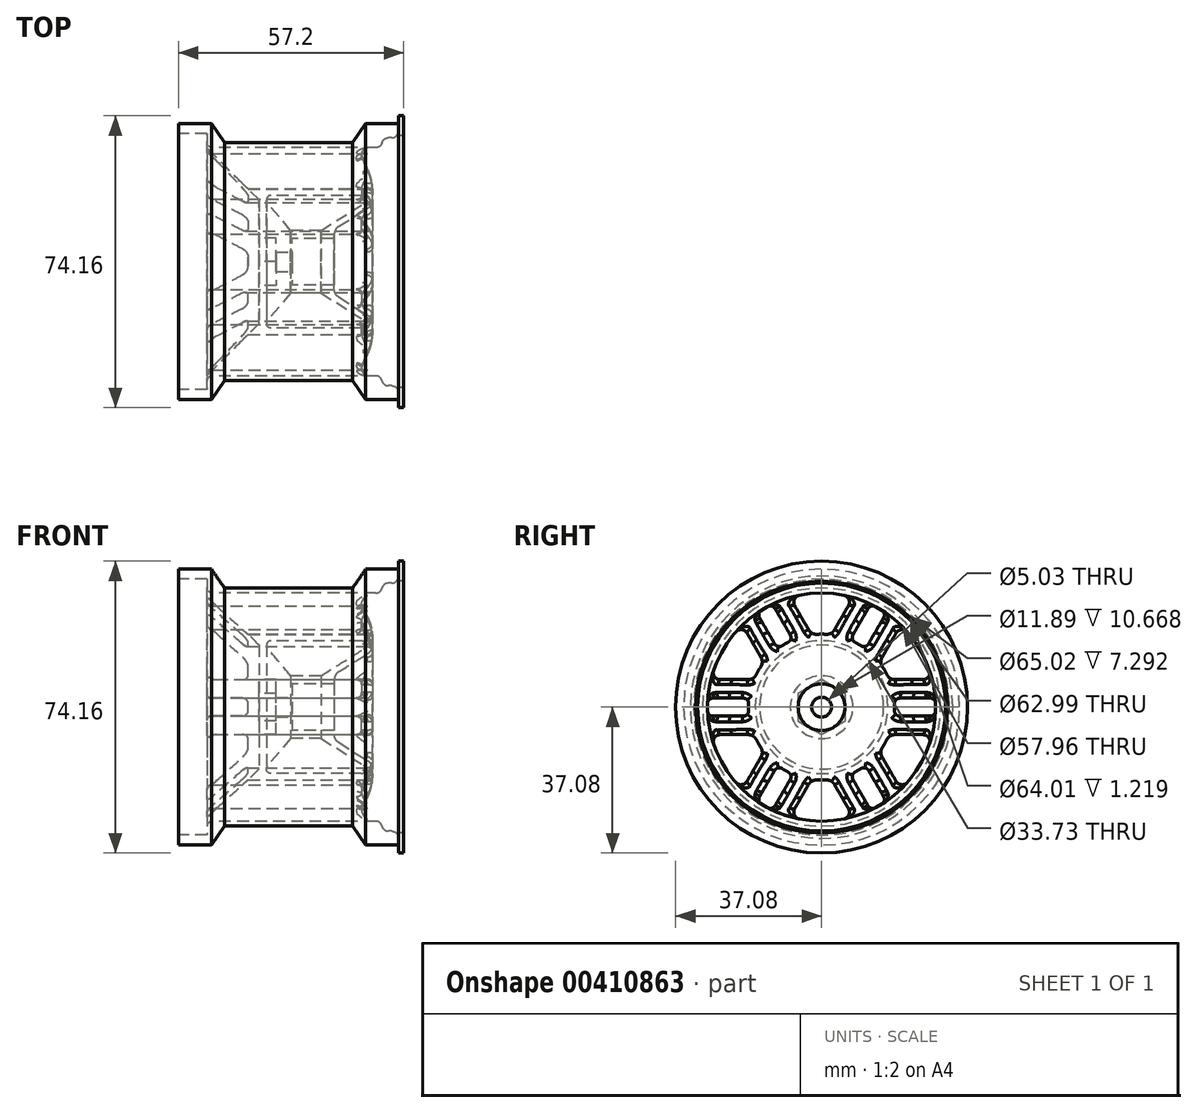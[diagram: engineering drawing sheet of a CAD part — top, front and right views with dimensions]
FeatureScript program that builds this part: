
annotation { "Feature Type Name" : "Feature", "Feature Type Description" : "" }
export const myFeature = defineFeature(function(context is Context, id is Id, definition is map)
    precondition{}
    {
        {
            var Q0;
            Q0=qCreatedBy(makeId("Front.planeOp"),FACE);
            var sketch = newSketch(context, id + "F0", { "sketchPlane" : qUnion([Q0])});
            skLineSegment(sketch, "E0.top", {"start": v(-20.52, 0) * mm, "end": v(36.68, 0) * mm});
            skLineSegment(sketch, "E0.left", {"start": v(-20.52, 35.05) * mm, "end": v(-20.52, 0) * mm});
            skLineSegment(sketch, "E0.right", {"start": v(36.68, 35.05) * mm, "end": v(36.68, 0) * mm});
            skLineSegment(sketch, "E1.top", {"start": v(36.68, 37.08) * mm, "end": v(35.46, 37.08) * mm});
            skLineSegment(sketch, "E1.left", {"start": v(36.68, 35.05) * mm, "end": v(36.68, 37.08) * mm});
            skLineSegment(sketch, "E1.right", {"start": v(35.46, 35.05) * mm, "end": v(35.46, 37.08) * mm});
            skLineSegment(sketch, "E2", {"start": v(35.46, 35.05) * mm, "end": v(36.68, 35.05) * mm, "construction": true});
            skPoint(sketch, "E3", {"position": v(0, 0) * mm});
            skLineSegment(sketch, "E4", {"start": v(-20.52, 35.05) * mm, "end": v(-12.14, 35.05) * mm});
            skLineSegment(sketch, "E5", {"start": v(-12.14, 35.05) * mm, "end": v(-8.76, 30.23) * mm});
            skLineSegment(sketch, "E6", {"start": v(-8.76, 30.23) * mm, "end": v(23.7, 30.23) * mm});
            skLineSegment(sketch, "E7", {"start": v(23.7, 30.23) * mm, "end": v(27.08, 35.05) * mm});
            skLineSegment(sketch, "E8", {"start": v(27.08, 35.05) * mm, "end": v(35.46, 35.05) * mm});
            skLineSegment(sketch, "E9", {"start": v(7.47, 30.23) * mm, "end": v(7.47, 0) * mm, "construction": true});
            skSolve(sketch);
        }
        {
            var Q0;
            Q0=makeQuery(id+"F0.imprint","IMPRINT",FACE,{"disambiguationData":[TD([[makeQuery(id+"F0.imprint","IMPRINT",EDGE,{"derivedFrom":sQuery(id+"F0.wireOp",EDGE,"E0.top")}),1.0]])]});
            var Q1;
            Q1=sQuery(id+"F0.wireOp",EDGE,"E0.top");
            revolve(context, id + "F1", {"entities" : qUnion([Q0]), "axis" : qUnion([Q1]), "revolveType" : RevolveType.FULL});
        }
        {
            var Q0;
            Q0=qCreatedBy(makeId("Right.planeOp"),FACE);
            cPlane(context, id + "F2", {"entities" : qUnion([Q0]), "cplaneType" : CPlaneType.OFFSET, "offset" : 13.2 * mm, "width" : 152.4 * mm, "height" : 152.4 * mm});
        }
        {
            var Q0;
            Q0=qCreatedBy(id+"F2.planeOp",FACE);
            var sketch = newSketch(context, id + "F3", { "sketchPlane" : qUnion([Q0])});
            skPoint(sketch, "E10", {"position": v(0, 0) * mm});
            skSolve(sketch);
        }
        {
            var Q0;
            Q0=sQuery(id+"F3.wireOp",VERTEX,"E10");
            var Q1;
            Q1=makeQuery(id+"F1.opRevolve","SWEPT_BODY",BODY,{"disambiguationData":[OSD([sQuery(id+"F0.wireOp",EDGE,"E0.top"),sQuery(id+"F0.wireOp",EDGE,"E0.left"),sQuery(id+"F0.wireOp",EDGE,"E0.right"),sQuery(id+"F0.wireOp",EDGE,"E1.top"),sQuery(id+"F0.wireOp",EDGE,"E1.left"),sQuery(id+"F0.wireOp",EDGE,"E1.right"),sQuery(id+"F0.wireOp",EDGE,"E4"),sQuery(id+"F0.wireOp",EDGE,"E5"),sQuery(id+"F0.wireOp",EDGE,"E6"),sQuery(id+"F0.wireOp",EDGE,"E7"),sQuery(id+"F0.wireOp",EDGE,"E8")])]});
            hole(context, id + "F4", {"style" : HoleStyle.SIMPLE, "endStyle" : HoleEndStyle.THROUGH, "oppositeDirection" : true, "holeDiameter" : 11.9 * mm, "locations" : qUnion([Q0]), "scope" : qUnion([Q1]), "isTappedThrough" : true});
        }
        {
            var Q0;
            Q0=sQuery(id+"F3.wireOp",VERTEX,"E10");
            var Q1;
            Q1=makeQuery(id+"F1.opRevolve","SWEPT_BODY",BODY,{"disambiguationData":[OSD([sQuery(id+"F0.wireOp",EDGE,"E0.top"),sQuery(id+"F0.wireOp",EDGE,"E0.left"),sQuery(id+"F0.wireOp",EDGE,"E0.right"),sQuery(id+"F0.wireOp",EDGE,"E1.top"),sQuery(id+"F0.wireOp",EDGE,"E1.left"),sQuery(id+"F0.wireOp",EDGE,"E1.right"),sQuery(id+"F0.wireOp",EDGE,"E4"),sQuery(id+"F0.wireOp",EDGE,"E5"),sQuery(id+"F0.wireOp",EDGE,"E6"),sQuery(id+"F0.wireOp",EDGE,"E7"),sQuery(id+"F0.wireOp",EDGE,"E8")])]});
            hole(context, id + "F5", {"style" : HoleStyle.C_BORE, "endStyle" : HoleEndStyle.THROUGH, "holeDiameter" : 5.03 * mm, "cBoreDiameter" : 11.9 * mm, "cBoreDepth" : 4.83 * mm, "locations" : qUnion([Q0]), "scope" : qUnion([Q1]), "isTappedThrough" : true});
        }
        {
            var Q0;
            Q0=qCreatedBy(makeId("Front.planeOp"),FACE);
            var sketch = newSketch(context, id + "F6", { "sketchPlane" : qUnion([Q0])});
            skLineSegment(sketch, "E11.bottom", {"start": v(0, 0) * mm, "end": v(-20.52, 0) * mm});
            skLineSegment(sketch, "E11.left", {"start": v(0, 0) * mm, "end": v(0, 15.75) * mm});
            skLineSegment(sketch, "E11.right", {"start": v(-20.52, 0) * mm, "end": v(-20.52, 32.51) * mm});
            skLineSegment(sketch, "E12", {"start": v(-20.52, 32.51) * mm, "end": v(-20.52, 35.05) * mm, "construction": true});
            skPoint(sketch, "E13.visualSharp", {"position": v(0, 15.75) * mm});
            skPoint(sketch, "E14.visualSharp", {"position": v(-20.52, 32.51) * mm});
            skLineSegment(sketch, "E15", {"start": v(-13.23, 28.98) * mm, "end": v(0, 15.75) * mm});
            skLineSegment(sketch, "E16", {"start": v(-20.52, 32.51) * mm, "end": v(-13.23, 32.51) * mm});
            skLineSegment(sketch, "E17", {"start": v(-13.23, 32.51) * mm, "end": v(-13.23, 28.98) * mm});
            skSolve(sketch);
        }
        {
            var Q0;
            Q0=qSketchRegion(id+"F6",true);
            var Q1;
            Q1=sQuery(id+"F6.wireOp",EDGE,"E11.bottom");
            revolve(context, id + "F7", {"operationType" : NewBodyOperationType.REMOVE, "entities" : qUnion([Q0]), "axis" : qUnion([Q1]), "revolveType" : RevolveType.FULL, "oppositeDirection" : true});
        }
        {
            var Q0;
            Q0=qCreatedBy(makeId("Right.planeOp"),FACE);
            var sketch = newSketch(context, id + "F8", { "sketchPlane" : qUnion([Q0])});
            skPoint(sketch, "E18", {"position": v(0.13, 0.17) * mm});
            skLineSegment(sketch, "E19", {"start": v(6.05, -3.5) * mm, "end": v(6.05, 3.5) * mm});
            skLineSegment(sketch, "E20", {"start": v(0, 0) * mm, "end": v(6.05, 0) * mm, "construction": true});
            skLineSegment(sketch, "E21.1.0", {"start": v(6.05, 3.5) * mm, "end": v(0, 6.98) * mm});
            skLineSegment(sketch, "E21.2.0", {"start": v(0, 6.98) * mm, "end": v(-6.05, 3.5) * mm});
            skLineSegment(sketch, "E21.3.0", {"start": v(-6.05, 3.5) * mm, "end": v(-6.05, -3.5) * mm});
            skLineSegment(sketch, "E21.4.0", {"start": v(-6.05, -3.5) * mm, "end": v(0, -6.98) * mm});
            skLineSegment(sketch, "E21.5.0", {"start": v(0, -6.98) * mm, "end": v(6.05, -3.5) * mm});
            skPoint(sketch, "E21.center", {"position": v(0, 0) * mm});
            skPoint(sketch, "E22.orphan", {"position": v(1.46, 7.82) * mm});
            skPoint(sketch, "E23.orphan", {"position": v(6.05, 5.17) * mm});
            skPoint(sketch, "E24.orphan", {"position": v(6.05, -5.17) * mm});
            skPoint(sketch, "E25.orphan", {"position": v(-1.46, 7.82) * mm});
            skPoint(sketch, "E26.orphan", {"position": v(7.5, 2.65) * mm});
            skPoint(sketch, "E27.orphan", {"position": v(7.5, -2.65) * mm});
            skPoint(sketch, "E28.orphan", {"position": v(1.46, -7.82) * mm});
            skPoint(sketch, "E29.orphan", {"position": v(-1.46, -7.82) * mm});
            skPoint(sketch, "E30.orphan", {"position": v(-6.05, -5.17) * mm});
            skPoint(sketch, "E31.orphan", {"position": v(-7.5, -2.65) * mm});
            skPoint(sketch, "E32.orphan", {"position": v(-7.5, 2.65) * mm});
            skPoint(sketch, "E33.orphan", {"position": v(-6.05, 5.17) * mm});
            skSolve(sketch);
        }
        {
            var Q0;
            Q0=qSketchRegion(id+"F8",true);
            extrude(context, id + "F9", {"entities" : qUnion([Q0]), "operationType" : NewBodyOperationType.REMOVE, "depth" : 4.32 * mm});
        }
        {
            var Q0;
            Q0=qCreatedBy(makeId("Front.planeOp"),FACE);
            var sketch = newSketch(context, id + "F10", { "sketchPlane" : qUnion([Q0])});
            skLineSegment(sketch, "E34", {"start": v(36.68, 32) * mm, "end": v(36.68, 37.08) * mm, "construction": true});
            skLineSegment(sketch, "E35", {"start": v(36.68, 32) * mm, "end": v(35.46, 32) * mm});
            skLineSegment(sketch, "E36", {"start": v(35.46, 32) * mm, "end": v(35.32, 33.33) * mm});
            skArc(sketch, "E37", {"start": v(35.32, 33.33) * mm, "mid": v(34.9, 32.04) * mm, "end": v(33.67, 31.5) * mm});
            skLineSegment(sketch, "E38", {"start": v(33.67, 31.5) * mm, "end": v(32.8, 31.5) * mm});
            skArc(sketch, "E39", {"start": v(32.8, 31.5) * mm, "mid": v(31.79, 31.14) * mm, "end": v(31.2, 30.24) * mm});
            skArc(sketch, "E40", {"start": v(29.59, 28.98) * mm, "mid": v(30.6, 29.33) * mm, "end": v(31.2, 30.24) * mm});
            skLineSegment(sketch, "E41", {"start": v(29.59, 28.98) * mm, "end": v(27.56, 28.98) * mm});
            skArc(sketch, "E42", {"start": v(27.56, 28.98) * mm, "mid": v(26.28, 28.29) * mm, "end": v(26.17, 26.83) * mm});
            skLineSegment(sketch, "E43", {"start": v(8.38, 5.94) * mm, "end": v(19.05, 5.94) * mm, "construction": true});
            skLineSegment(sketch, "E44", {"start": v(27.55, 23.75) * mm, "end": v(26.17, 26.83) * mm});
            skLineSegment(sketch, "E45", {"start": v(36.68, 32) * mm, "end": v(36.68, 0) * mm});
            skLineSegment(sketch, "E46", {"start": v(36.68, 0) * mm, "end": v(19.05, 0) * mm});
            skLineSegment(sketch, "E47", {"start": v(31.2, 30.24) * mm, "end": v(30.65, 28.06) * mm, "construction": true});
            skLineSegment(sketch, "E48", {"start": v(19.05, 5.94) * mm, "end": v(19.05, 6.86) * mm});
            skPoint(sketch, "E49.visualSharp", {"position": v(19.05, 6.86) * mm});
            skArc(sketch, "E49.filletArc", {"start": v(28.77, 18.03) * mm, "mid": v(28.46, 20.96) * mm, "end": v(27.55, 23.75) * mm});
            skLineSegment(sketch, "E50", {"start": v(28.77, 18.03) * mm, "end": v(28.77, 15.75) * mm});
            skLineSegment(sketch, "E51", {"start": v(20.24, 9.01) * mm, "end": v(27.58, 13.6) * mm});
            skArc(sketch, "E52", {"start": v(28.77, 15.75) * mm, "mid": v(28.45, 14.52) * mm, "end": v(27.58, 13.6) * mm});
            skArc(sketch, "E53", {"start": v(20.24, 9.01) * mm, "mid": v(19.37, 8.09) * mm, "end": v(19.05, 6.86) * mm});
            skLineSegment(sketch, "E54", {"start": v(19.05, 5.94) * mm, "end": v(19.05, 0) * mm});
            skSolve(sketch);
        }
        {
            var Q0;
            Q0=qSketchRegion(id+"F10",true);
            var Q1;
            Q1=sQuery(id+"F10.wireOp",EDGE,"E46");
            revolve(context, id + "F11", {"operationType" : NewBodyOperationType.REMOVE, "entities" : qUnion([Q0]), "axis" : qUnion([Q1]), "revolveType" : RevolveType.FULL, "oppositeDirection" : true});
        }
        {
            var Q0;
            Q0=makeQuery(id+"F1.opRevolve","SWEPT_FACE",FACE,{"disambiguationData":[OSD([sQuery(id+"F0.wireOp",EDGE,"E0.right"),sQuery(id+"F0.wireOp",EDGE,"E1.left")])]});
            cPlane(context, id + "F12", {"entities" : qUnion([Q0]), "cplaneType" : CPlaneType.OFFSET, "offset" : 0 * mm, "width" : 152.4 * mm, "height" : 152.4 * mm});
        }
        {
            var Q0;
            Q0=qCreatedBy(id+"F12.planeOp",FACE);
            var sketch = newSketch(context, id + "F13", { "sketchPlane" : qUnion([Q0])});
            skLineSegment(sketch, "E55", {"start": v(6.83, 25.8) * mm, "end": v(3.28, 19.64) * mm});
            skLineSegment(sketch, "E56", {"start": v(0, 28.98) * mm, "end": v(0, 18.54) * mm, "construction": true});
            skArc(sketch, "E57", {"start": v(5.63, 28.43) * mm, "mid": v(2.83, 28.84) * mm, "end": v(0, 28.98) * mm});
            skArc(sketch, "E58", {"start": v(5.63, 28.43) * mm, "mid": v(6.9, 27.42) * mm, "end": v(6.83, 25.8) * mm});
            skLineSegment(sketch, "E59", {"start": v(0, 0) * mm, "end": v(0, 13.97) * mm, "construction": true});
            skArc(sketch, "E60", {"start": v(0, 18.54) * mm, "mid": v(0.58, 18.53) * mm, "end": v(1.15, 18.5) * mm});
            skArc(sketch, "E61.filletArc", {"start": v(1.15, 18.5) * mm, "mid": v(2.38, 18.77) * mm, "end": v(3.28, 19.64) * mm});
            skArc(sketch, "E62.MirrorCS", {"start": v(0, 18.54) * mm, "mid": v(-0.58, 18.53) * mm, "end": v(-1.15, 18.5) * mm});
            skArc(sketch, "E63.MirrorCS", {"start": v(-1.15, 18.5) * mm, "mid": v(-2.38, 18.77) * mm, "end": v(-3.28, 19.64) * mm});
            skLineSegment(sketch, "E64.MirrorCS", {"start": v(-6.83, 25.8) * mm, "end": v(-3.28, 19.64) * mm});
            skArc(sketch, "E65.MirrorCS", {"start": v(-5.63, 28.43) * mm, "mid": v(-6.9, 27.42) * mm, "end": v(-6.83, 25.8) * mm});
            skArc(sketch, "E66.MirrorCS", {"start": v(-5.63, 28.43) * mm, "mid": v(-2.83, 28.84) * mm, "end": v(0, 28.98) * mm});
            skLineSegment(sketch, "E67", {"start": v(0, 13.97) * mm, "end": v(3.28, 19.64) * mm, "construction": true});
            skSolve(sketch);
        }
        {
            var Q0;
            Q0=qSketchRegion(id+"F13",true);
            extrude(context, id + "F14", {"entities" : qUnion([Q0]), "endBound" : BoundingType.THROUGH_ALL, "oppositeDirection" : true, "depth" : 71.11 * mm});
        }
        {
            var Q0;
            Q0=makeQuery(id+"F14.opExtrude","SWEPT_BODY",BODY,{"disambiguationData":[OSD([sQuery(id+"F13.wireOp",EDGE,"E55"),sQuery(id+"F13.wireOp",EDGE,"E57"),sQuery(id+"F13.wireOp",EDGE,"E58"),sQuery(id+"F13.wireOp",EDGE,"E60"),sQuery(id+"F13.wireOp",EDGE,"E61.filletArc"),sQuery(id+"F13.wireOp",EDGE,"E62.MirrorCS"),sQuery(id+"F13.wireOp",EDGE,"E63.MirrorCS"),sQuery(id+"F13.wireOp",EDGE,"E64.MirrorCS"),sQuery(id+"F13.wireOp",EDGE,"E65.MirrorCS"),sQuery(id+"F13.wireOp",EDGE,"E66.MirrorCS")])]});
            var Q1;
            Q1=sQuery(id+"F0.wireOp",EDGE,"E0.top");
            circularPattern(context, id + "F15", {"operationType" : NewBodyOperationType.REMOVE, "entities" : qUnion([Q0]), "axis" : qUnion([Q1]), "angle" : 360 * degree, "instanceCount" : 6, "equalSpace" : true});
        }
        {
            var Q0;
            Q0=makeQuery(id+"F15.boolean.opBoolean","SPLIT",FACE,{"disambiguationData":[TD([makeQuery(id+"F15.opPattern","COPY",FACE,{"derivedFrom":makeQuery(id+"F14.opExtrude","SWEPT_FACE",FACE,{"disambiguationData":[OSD([sQuery(id+"F13.wireOp",EDGE,"E55")])]}),"instanceName":"2"})])],"derivedFrom":makeQuery(id+"F11.boolean.opBoolean","COPY",FACE,{"derivedFrom":makeQuery(id+"F11.opRevolve","SWEPT_FACE",FACE,{"disambiguationData":[OSD([sQuery(id+"F10.wireOp",EDGE,"E44")])]})})});
            var Q1;
            Q1=makeQuery(id+"F15.boolean.opBoolean","SPLIT",FACE,{"disambiguationData":[TD([makeQuery(id+"F15.opPattern","COPY",FACE,{"derivedFrom":makeQuery(id+"F14.opExtrude","SWEPT_FACE",FACE,{"disambiguationData":[OSD([sQuery(id+"F13.wireOp",EDGE,"E55")])]}),"instanceName":"2"})])],"derivedFrom":makeQuery(id+"F11.boolean.opBoolean","COPY",FACE,{"derivedFrom":makeQuery(id+"F11.opRevolve","SWEPT_FACE",FACE,{"disambiguationData":[OSD([sQuery(id+"F10.wireOp",EDGE,"E49.filletArc")])]})})});
            var Q2;
            Q2=makeQuery(id+"F15.boolean.opBoolean","SPLIT",FACE,{"disambiguationData":[TD([makeQuery(id+"F15.opPattern","COPY",FACE,{"derivedFrom":makeQuery(id+"F14.opExtrude","SWEPT_FACE",FACE,{"disambiguationData":[OSD([sQuery(id+"F13.wireOp",EDGE,"E58")])]}),"instanceName":"2"})])],"derivedFrom":makeQuery(id+"F11.boolean.opBoolean","COPY",FACE,{"derivedFrom":makeQuery(id+"F11.opRevolve","SWEPT_FACE",FACE,{"disambiguationData":[OSD([sQuery(id+"F10.wireOp",EDGE,"E42")])]})})});
            var Q3;
            Q3=makeQuery(id+"F15.boolean.opBoolean","SPLIT",FACE,{"disambiguationData":[TD([makeQuery(id+"F15.opPattern","COPY",FACE,{"derivedFrom":makeQuery(id+"F14.opExtrude","SWEPT_FACE",FACE,{"disambiguationData":[OSD([sQuery(id+"F13.wireOp",EDGE,"E55")])]}),"instanceName":"1"})])],"derivedFrom":makeQuery(id+"F11.boolean.opBoolean","COPY",FACE,{"derivedFrom":makeQuery(id+"F11.opRevolve","SWEPT_FACE",FACE,{"disambiguationData":[OSD([sQuery(id+"F10.wireOp",EDGE,"E44")])]})})});
            var Q4;
            Q4=makeQuery(id+"F15.boolean.opBoolean","SPLIT",FACE,{"disambiguationData":[TD([makeQuery(id+"F15.opPattern","COPY",FACE,{"derivedFrom":makeQuery(id+"F14.opExtrude","SWEPT_FACE",FACE,{"disambiguationData":[OSD([sQuery(id+"F13.wireOp",EDGE,"E55")])]}),"instanceName":"1"})])],"derivedFrom":makeQuery(id+"F11.boolean.opBoolean","COPY",FACE,{"derivedFrom":makeQuery(id+"F11.opRevolve","SWEPT_FACE",FACE,{"disambiguationData":[OSD([sQuery(id+"F10.wireOp",EDGE,"E49.filletArc")])]})})});
            var Q5;
            Q5=makeQuery(id+"F15.boolean.opBoolean","SPLIT",FACE,{"disambiguationData":[TD([makeQuery(id+"F15.opPattern","COPY",FACE,{"derivedFrom":makeQuery(id+"F14.opExtrude","SWEPT_FACE",FACE,{"disambiguationData":[OSD([sQuery(id+"F13.wireOp",EDGE,"E58")])]}),"instanceName":"1"})])],"derivedFrom":makeQuery(id+"F11.boolean.opBoolean","COPY",FACE,{"derivedFrom":makeQuery(id+"F11.opRevolve","SWEPT_FACE",FACE,{"disambiguationData":[OSD([sQuery(id+"F10.wireOp",EDGE,"E42")])]})})});
            var Q6;
            Q6=makeQuery(id+"F15.boolean.opBoolean","SPLIT",FACE,{"disambiguationData":[TD([makeQuery(id+"F15.opPattern","COPY",FACE,{"derivedFrom":makeQuery(id+"F14.opExtrude","SWEPT_FACE",FACE,{"disambiguationData":[OSD([sQuery(id+"F13.wireOp",EDGE,"E55")])]}),"instanceName":"3"})])],"derivedFrom":makeQuery(id+"F11.boolean.opBoolean","COPY",FACE,{"derivedFrom":makeQuery(id+"F11.opRevolve","SWEPT_FACE",FACE,{"disambiguationData":[OSD([sQuery(id+"F10.wireOp",EDGE,"E44")])]})})});
            var Q7;
            Q7=makeQuery(id+"F11.boolean.opBoolean","COPY",FACE,{"derivedFrom":makeQuery(id+"F11.opRevolve","SWEPT_FACE",FACE,{"disambiguationData":[OSD([sQuery(id+"F10.wireOp",EDGE,"E50")])]})});
            var Q8;
            Q8=makeQuery(id+"F15.boolean.opBoolean","SPLIT",FACE,{"disambiguationData":[TD([makeQuery(id+"F15.opPattern","COPY",FACE,{"derivedFrom":makeQuery(id+"F14.opExtrude","SWEPT_FACE",FACE,{"disambiguationData":[OSD([sQuery(id+"F13.wireOp",EDGE,"E55")])]}),"instanceName":"3"})])],"derivedFrom":makeQuery(id+"F11.boolean.opBoolean","COPY",FACE,{"derivedFrom":makeQuery(id+"F11.opRevolve","SWEPT_FACE",FACE,{"disambiguationData":[OSD([sQuery(id+"F10.wireOp",EDGE,"E49.filletArc")])]})})});
            var Q9;
            Q9=makeQuery(id+"F15.boolean.opBoolean","SPLIT",FACE,{"disambiguationData":[TD([makeQuery(id+"F15.opPattern","COPY",FACE,{"derivedFrom":makeQuery(id+"F14.opExtrude","SWEPT_FACE",FACE,{"disambiguationData":[OSD([sQuery(id+"F13.wireOp",EDGE,"E58")])]}),"instanceName":"3"})])],"derivedFrom":makeQuery(id+"F11.boolean.opBoolean","COPY",FACE,{"derivedFrom":makeQuery(id+"F11.opRevolve","SWEPT_FACE",FACE,{"disambiguationData":[OSD([sQuery(id+"F10.wireOp",EDGE,"E42")])]})})});
            var Q10;
            Q10=makeQuery(id+"F15.boolean.opBoolean","SPLIT",FACE,{"disambiguationData":[TD([makeQuery(id+"F15.opPattern","COPY",FACE,{"derivedFrom":makeQuery(id+"F14.opExtrude","SWEPT_FACE",FACE,{"disambiguationData":[OSD([sQuery(id+"F13.wireOp",EDGE,"E55")])]}),"instanceName":"4"})])],"derivedFrom":makeQuery(id+"F11.boolean.opBoolean","COPY",FACE,{"derivedFrom":makeQuery(id+"F11.opRevolve","SWEPT_FACE",FACE,{"disambiguationData":[OSD([sQuery(id+"F10.wireOp",EDGE,"E49.filletArc")])]})})});
            var Q11;
            Q11=makeQuery(id+"F15.boolean.opBoolean","SPLIT",FACE,{"disambiguationData":[TD([makeQuery(id+"F15.opPattern","COPY",FACE,{"derivedFrom":makeQuery(id+"F14.opExtrude","SWEPT_FACE",FACE,{"disambiguationData":[OSD([sQuery(id+"F13.wireOp",EDGE,"E55")])]}),"instanceName":"4"})])],"derivedFrom":makeQuery(id+"F11.boolean.opBoolean","COPY",FACE,{"derivedFrom":makeQuery(id+"F11.opRevolve","SWEPT_FACE",FACE,{"disambiguationData":[OSD([sQuery(id+"F10.wireOp",EDGE,"E44")])]})})});
            var Q12;
            Q12=makeQuery(id+"F15.boolean.opBoolean","SPLIT",FACE,{"disambiguationData":[TD([makeQuery(id+"F15.opPattern","COPY",FACE,{"derivedFrom":makeQuery(id+"F14.opExtrude","SWEPT_FACE",FACE,{"disambiguationData":[OSD([sQuery(id+"F13.wireOp",EDGE,"E58")])]}),"instanceName":"4"})])],"derivedFrom":makeQuery(id+"F11.boolean.opBoolean","COPY",FACE,{"derivedFrom":makeQuery(id+"F11.opRevolve","SWEPT_FACE",FACE,{"disambiguationData":[OSD([sQuery(id+"F10.wireOp",EDGE,"E42")])]})})});
            var Q13;
            Q13=makeQuery(id+"F15.boolean.opBoolean","SPLIT",FACE,{"disambiguationData":[TD([makeQuery(id+"F14.opExtrude","SWEPT_FACE",FACE,{"disambiguationData":[OSD([sQuery(id+"F13.wireOp",EDGE,"E63.MirrorCS")])]})])],"derivedFrom":makeQuery(id+"F11.boolean.opBoolean","COPY",FACE,{"derivedFrom":makeQuery(id+"F11.opRevolve","SWEPT_FACE",FACE,{"disambiguationData":[OSD([sQuery(id+"F10.wireOp",EDGE,"E49.filletArc")])]})})});
            var Q14;
            Q14=makeQuery(id+"F15.boolean.opBoolean","SPLIT",FACE,{"disambiguationData":[TD([makeQuery(id+"F14.opExtrude","SWEPT_FACE",FACE,{"disambiguationData":[OSD([sQuery(id+"F13.wireOp",EDGE,"E64.MirrorCS")])]})])],"derivedFrom":makeQuery(id+"F11.boolean.opBoolean","COPY",FACE,{"derivedFrom":makeQuery(id+"F11.opRevolve","SWEPT_FACE",FACE,{"disambiguationData":[OSD([sQuery(id+"F10.wireOp",EDGE,"E44")])]})})});
            var Q15;
            Q15=makeQuery(id+"F15.boolean.opBoolean","SPLIT",FACE,{"disambiguationData":[TD([makeQuery(id+"F14.opExtrude","SWEPT_FACE",FACE,{"disambiguationData":[OSD([sQuery(id+"F13.wireOp",EDGE,"E65.MirrorCS")])]})])],"derivedFrom":makeQuery(id+"F11.boolean.opBoolean","COPY",FACE,{"derivedFrom":makeQuery(id+"F11.opRevolve","SWEPT_FACE",FACE,{"disambiguationData":[OSD([sQuery(id+"F10.wireOp",EDGE,"E42")])]})})});
            var Q16;
            Q16=makeQuery(id+"F15.boolean.opBoolean","SPLIT",FACE,{"disambiguationData":[TD([makeQuery(id+"F14.opExtrude","SWEPT_FACE",FACE,{"disambiguationData":[OSD([sQuery(id+"F13.wireOp",EDGE,"E55")])]})])],"derivedFrom":makeQuery(id+"F11.boolean.opBoolean","COPY",FACE,{"derivedFrom":makeQuery(id+"F11.opRevolve","SWEPT_FACE",FACE,{"disambiguationData":[OSD([sQuery(id+"F10.wireOp",EDGE,"E44")])]})})});
            var Q17;
            Q17=makeQuery(id+"F15.boolean.opBoolean","SPLIT",FACE,{"disambiguationData":[TD([makeQuery(id+"F14.opExtrude","SWEPT_FACE",FACE,{"disambiguationData":[OSD([sQuery(id+"F13.wireOp",EDGE,"E55")])]})])],"derivedFrom":makeQuery(id+"F11.boolean.opBoolean","COPY",FACE,{"derivedFrom":makeQuery(id+"F11.opRevolve","SWEPT_FACE",FACE,{"disambiguationData":[OSD([sQuery(id+"F10.wireOp",EDGE,"E49.filletArc")])]})})});
            var Q18;
            Q18=makeQuery(id+"F15.boolean.opBoolean","SPLIT",FACE,{"disambiguationData":[TD([makeQuery(id+"F14.opExtrude","SWEPT_FACE",FACE,{"disambiguationData":[OSD([sQuery(id+"F13.wireOp",EDGE,"E58")])]})])],"derivedFrom":makeQuery(id+"F11.boolean.opBoolean","COPY",FACE,{"derivedFrom":makeQuery(id+"F11.opRevolve","SWEPT_FACE",FACE,{"disambiguationData":[OSD([sQuery(id+"F10.wireOp",EDGE,"E42")])]})})});
            var Q19;
            Q19=makeQuery(id+"F15.boolean.opBoolean","SPLIT",FACE,{"disambiguationData":[TD([makeQuery(id+"F15.opPattern","COPY",FACE,{"derivedFrom":makeQuery(id+"F14.opExtrude","SWEPT_FACE",FACE,{"disambiguationData":[OSD([sQuery(id+"F13.wireOp",EDGE,"E64.MirrorCS")])]}),"instanceName":"4"})])],"derivedFrom":makeQuery(id+"F11.boolean.opBoolean","COPY",FACE,{"derivedFrom":makeQuery(id+"F11.opRevolve","SWEPT_FACE",FACE,{"disambiguationData":[OSD([sQuery(id+"F10.wireOp",EDGE,"E44")])]})})});
            var Q20;
            Q20=makeQuery(id+"F15.boolean.opBoolean","SPLIT",FACE,{"disambiguationData":[TD([makeQuery(id+"F15.opPattern","COPY",FACE,{"derivedFrom":makeQuery(id+"F14.opExtrude","SWEPT_FACE",FACE,{"disambiguationData":[OSD([sQuery(id+"F13.wireOp",EDGE,"E65.MirrorCS")])]}),"instanceName":"4"})])],"derivedFrom":makeQuery(id+"F11.boolean.opBoolean","COPY",FACE,{"derivedFrom":makeQuery(id+"F11.opRevolve","SWEPT_FACE",FACE,{"disambiguationData":[OSD([sQuery(id+"F10.wireOp",EDGE,"E42")])]})})});
            fillet(context, id + "F16", {"entities" : qUnion([Q0, Q1, Q2, Q3, Q4, Q5, Q6, Q7, Q8, Q9, Q10, Q11, Q12, Q13, Q14, Q15, Q16, Q17, Q18, Q19, Q20]), "radius" : 1.37 * mm, "allowEdgeOverflow" : false});
        }
        {
            var Q0;
            Q0=qCreatedBy(id+"F12.planeOp",FACE);
            var sketch = newSketch(context, id + "F17", { "sketchPlane" : qUnion([Q0])});
            skPoint(sketch, "E68", {"position": v(0, 0) * mm});
            skLineSegment(sketch, "E69", {"start": v(0, 0) * mm, "end": v(16.02, 27.74) * mm, "construction": true});
            skLineSegment(sketch, "E70", {"start": v(11.93, 16.08) * mm, "end": v(15.78, 22.75) * mm});
            skArc(sketch, "E71", {"start": v(9.27, 16.06) * mm, "mid": v(9.64, 15.84) * mm, "end": v(10, 15.62) * mm});
            skArc(sketch, "E72", {"start": v(14.5, 25.1) * mm, "mid": v(14.9, 24.86) * mm, "end": v(15.31, 24.6) * mm});
            skPoint(sketch, "E73.visualSharp", {"position": v(16.43, 23.88) * mm});
            skArc(sketch, "E73.filletArc", {"start": v(15.78, 22.75) * mm, "mid": v(15.92, 23.77) * mm, "end": v(15.31, 24.6) * mm});
            skPoint(sketch, "E74.visualSharp", {"position": v(11.18, 14.8) * mm});
            skArc(sketch, "E74.filletArc", {"start": v(10, 15.62) * mm, "mid": v(11.06, 15.44) * mm, "end": v(11.93, 16.08) * mm});
            skArc(sketch, "E75.MirrorCS", {"start": v(9.27, 16.06) * mm, "mid": v(8.9, 16.27) * mm, "end": v(8.52, 16.47) * mm});
            skArc(sketch, "E76.MirrorCS", {"start": v(8.52, 16.47) * mm, "mid": v(7.84, 17.3) * mm, "end": v(7.97, 18.37) * mm});
            skLineSegment(sketch, "E77.MirrorCS", {"start": v(7.97, 18.37) * mm, "end": v(11.82, 25.04) * mm});
            skArc(sketch, "E78.MirrorCS", {"start": v(11.82, 25.04) * mm, "mid": v(12.63, 25.67) * mm, "end": v(13.65, 25.56) * mm});
            skArc(sketch, "E79.MirrorCS", {"start": v(14.5, 25.1) * mm, "mid": v(14.07, 25.34) * mm, "end": v(13.65, 25.56) * mm});
            skSolve(sketch);
        }
        {
            var Q0;
            Q0=qSketchRegion(id+"F17",true);
            extrude(context, id + "F18", {"entities" : qUnion([Q0]), "endBound" : BoundingType.THROUGH_ALL, "oppositeDirection" : true, "depth" : 25.4 * mm});
        }
        {
            var Q0;
            Q0=makeQuery(id+"F18.opExtrude","SWEPT_BODY",BODY,{"disambiguationData":[OSD([sQuery(id+"F17.wireOp",EDGE,"E70"),sQuery(id+"F17.wireOp",EDGE,"E71"),sQuery(id+"F17.wireOp",EDGE,"E72"),sQuery(id+"F17.wireOp",EDGE,"E73.filletArc"),sQuery(id+"F17.wireOp",EDGE,"E74.filletArc"),sQuery(id+"F17.wireOp",EDGE,"E75.MirrorCS"),sQuery(id+"F17.wireOp",EDGE,"E76.MirrorCS"),sQuery(id+"F17.wireOp",EDGE,"E77.MirrorCS"),sQuery(id+"F17.wireOp",EDGE,"E78.MirrorCS"),sQuery(id+"F17.wireOp",EDGE,"E79.MirrorCS")])]});
            var Q1;
            Q1=sQuery(id+"F0.wireOp",EDGE,"E0.top");
            circularPattern(context, id + "F19", {"operationType" : NewBodyOperationType.REMOVE, "entities" : qUnion([Q0]), "axis" : qUnion([Q1]), "angle" : 360 * degree, "instanceCount" : 6, "equalSpace" : true});
        }
        {
            var Q0;
            {var subQ2=sQuery(id+"F10.wireOp",EDGE,"E49.filletArc");var subQ3=makeQuery(id+"F11.boolean.opBoolean","COPY",FACE,{"derivedFrom":makeQuery(id+"F11.opRevolve","SWEPT_FACE",FACE,{"disambiguationData":[OSD([subQ2])]})});var subQ8=sQuery(id+"F13.wireOp",EDGE,"E55");var subQ9=makeQuery(id+"F15.opPattern","COPY",FACE,{"derivedFrom":makeQuery(id+"F14.opExtrude","SWEPT_FACE",FACE,{"disambiguationData":[OSD([subQ8])]}),"instanceName":"3"});Q0=makeQuery(id+"F19.boolean.opBoolean","SPLIT",FACE,{"disambiguationData":[TD([makeQuery(id+"F19.opPattern","COPY",FACE,{"derivedFrom":makeQuery(id+"F18.opExtrude","SWEPT_FACE",FACE,{"disambiguationData":[OSD([sQuery(id+"F17.wireOp",EDGE,"E76.MirrorCS")])]}),"instanceName":"3"})])],"derivedFrom":makeQuery(id+"F15.boolean.opBoolean","SPLIT",FACE,{"disambiguationData":[TD([subQ9])],"derivedFrom":subQ3})});}
            var Q1;
            {var subQ0=sQuery(id+"F13.wireOp",EDGE,"E58");var subQ1=makeQuery(id+"F15.opPattern","COPY",FACE,{"derivedFrom":makeQuery(id+"F14.opExtrude","SWEPT_FACE",FACE,{"disambiguationData":[OSD([subQ0])]}),"instanceName":"3"});var subQ2=sQuery(id+"F10.wireOp",EDGE,"E42");var subQ3=makeQuery(id+"F11.boolean.opBoolean","COPY",FACE,{"derivedFrom":makeQuery(id+"F11.opRevolve","SWEPT_FACE",FACE,{"disambiguationData":[OSD([subQ2])]})});Q1=makeQuery(id+"F19.boolean.opBoolean","SPLIT",FACE,{"disambiguationData":[TD([makeQuery(id+"F19.opPattern","COPY",FACE,{"derivedFrom":makeQuery(id+"F18.opExtrude","SWEPT_FACE",FACE,{"disambiguationData":[OSD([sQuery(id+"F17.wireOp",EDGE,"E77.MirrorCS")])]}),"instanceName":"3"})])],"derivedFrom":makeQuery(id+"F15.boolean.opBoolean","SPLIT",FACE,{"disambiguationData":[TD([subQ1])],"derivedFrom":subQ3})});}
            var Q2;
            {var subQ2=sQuery(id+"F10.wireOp",EDGE,"E49.filletArc");var subQ3=makeQuery(id+"F11.boolean.opBoolean","COPY",FACE,{"derivedFrom":makeQuery(id+"F11.opRevolve","SWEPT_FACE",FACE,{"disambiguationData":[OSD([subQ2])]})});Q2=makeQuery(id+"F19.boolean.opBoolean","SPLIT",FACE,{"disambiguationData":[TD([makeQuery(id+"F19.opPattern","COPY",FACE,{"derivedFrom":makeQuery(id+"F18.opExtrude","SWEPT_FACE",FACE,{"disambiguationData":[OSD([sQuery(id+"F17.wireOp",EDGE,"E74.filletArc")])]}),"instanceName":"3"})])],"derivedFrom":makeQuery(id+"F15.boolean.opBoolean","SPLIT",FACE,{"disambiguationData":[TD([makeQuery(id+"F15.opPattern","COPY",FACE,{"derivedFrom":makeQuery(id+"F14.opExtrude","SWEPT_FACE",FACE,{"disambiguationData":[OSD([sQuery(id+"F13.wireOp",EDGE,"E55")])]}),"instanceName":"3"})])],"derivedFrom":subQ3})});}
            var Q3;
            {var subQ2=sQuery(id+"F10.wireOp",EDGE,"E44");var subQ3=makeQuery(id+"F11.boolean.opBoolean","COPY",FACE,{"derivedFrom":makeQuery(id+"F11.opRevolve","SWEPT_FACE",FACE,{"disambiguationData":[OSD([subQ2])]})});Q3=makeQuery(id+"F19.boolean.opBoolean","SPLIT",FACE,{"disambiguationData":[TD([makeQuery(id+"F19.opPattern","COPY",FACE,{"derivedFrom":makeQuery(id+"F18.opExtrude","SWEPT_FACE",FACE,{"disambiguationData":[OSD([sQuery(id+"F17.wireOp",EDGE,"E70")])]}),"instanceName":"3"})])],"derivedFrom":makeQuery(id+"F15.boolean.opBoolean","SPLIT",FACE,{"disambiguationData":[TD([makeQuery(id+"F15.opPattern","COPY",FACE,{"derivedFrom":makeQuery(id+"F14.opExtrude","SWEPT_FACE",FACE,{"disambiguationData":[OSD([sQuery(id+"F13.wireOp",EDGE,"E55")])]}),"instanceName":"3"})])],"derivedFrom":subQ3})});}
            var Q4;
            {var subQ2=sQuery(id+"F10.wireOp",EDGE,"E42");var subQ3=makeQuery(id+"F11.boolean.opBoolean","COPY",FACE,{"derivedFrom":makeQuery(id+"F11.opRevolve","SWEPT_FACE",FACE,{"disambiguationData":[OSD([subQ2])]})});Q4=makeQuery(id+"F19.boolean.opBoolean","SPLIT",FACE,{"disambiguationData":[TD([makeQuery(id+"F19.opPattern","COPY",FACE,{"derivedFrom":makeQuery(id+"F18.opExtrude","SWEPT_FACE",FACE,{"disambiguationData":[OSD([sQuery(id+"F17.wireOp",EDGE,"E70")])]}),"instanceName":"3"})])],"derivedFrom":makeQuery(id+"F15.boolean.opBoolean","SPLIT",FACE,{"disambiguationData":[TD([makeQuery(id+"F15.opPattern","COPY",FACE,{"derivedFrom":makeQuery(id+"F14.opExtrude","SWEPT_FACE",FACE,{"disambiguationData":[OSD([sQuery(id+"F13.wireOp",EDGE,"E58")])]}),"instanceName":"3"})])],"derivedFrom":subQ3})});}
            var Q5;
            {var subQ2=sQuery(id+"F10.wireOp",EDGE,"E42");var subQ3=makeQuery(id+"F11.boolean.opBoolean","COPY",FACE,{"derivedFrom":makeQuery(id+"F11.opRevolve","SWEPT_FACE",FACE,{"disambiguationData":[OSD([subQ2])]})});Q5=makeQuery(id+"F19.boolean.opBoolean","SPLIT",FACE,{"disambiguationData":[TD([makeQuery(id+"F19.opPattern","COPY",FACE,{"derivedFrom":makeQuery(id+"F18.opExtrude","SWEPT_FACE",FACE,{"disambiguationData":[OSD([sQuery(id+"F17.wireOp",EDGE,"E77.MirrorCS")])]}),"instanceName":"1"})])],"derivedFrom":makeQuery(id+"F15.boolean.opBoolean","SPLIT",FACE,{"disambiguationData":[TD([makeQuery(id+"F14.opExtrude","SWEPT_FACE",FACE,{"disambiguationData":[OSD([sQuery(id+"F13.wireOp",EDGE,"E65.MirrorCS")])]})])],"derivedFrom":subQ3})});}
            var Q6;
            {var subQ4=sQuery(id+"F10.wireOp",EDGE,"E49.filletArc");var subQ5=makeQuery(id+"F11.boolean.opBoolean","COPY",FACE,{"derivedFrom":makeQuery(id+"F11.opRevolve","SWEPT_FACE",FACE,{"disambiguationData":[OSD([subQ4])]})});Q6=makeQuery(id+"F19.boolean.opBoolean","SPLIT",FACE,{"disambiguationData":[TD([makeQuery(id+"F19.opPattern","COPY",FACE,{"derivedFrom":makeQuery(id+"F18.opExtrude","SWEPT_FACE",FACE,{"disambiguationData":[OSD([sQuery(id+"F17.wireOp",EDGE,"E76.MirrorCS")])]}),"instanceName":"1"})])],"derivedFrom":makeQuery(id+"F15.boolean.opBoolean","SPLIT",FACE,{"disambiguationData":[TD([makeQuery(id+"F14.opExtrude","SWEPT_FACE",FACE,{"disambiguationData":[OSD([sQuery(id+"F13.wireOp",EDGE,"E63.MirrorCS")])]})])],"derivedFrom":subQ5})});}
            var Q7;
            {var subQ0=sQuery(id+"F13.wireOp",EDGE,"E63.MirrorCS");var subQ1=makeQuery(id+"F14.opExtrude","SWEPT_FACE",FACE,{"disambiguationData":[OSD([subQ0])]});var subQ2=sQuery(id+"F10.wireOp",EDGE,"E49.filletArc");var subQ3=makeQuery(id+"F11.boolean.opBoolean","COPY",FACE,{"derivedFrom":makeQuery(id+"F11.opRevolve","SWEPT_FACE",FACE,{"disambiguationData":[OSD([subQ2])]})});Q7=makeQuery(id+"F19.boolean.opBoolean","SPLIT",FACE,{"disambiguationData":[TD([makeQuery(id+"F19.opPattern","COPY",FACE,{"derivedFrom":makeQuery(id+"F18.opExtrude","SWEPT_FACE",FACE,{"disambiguationData":[OSD([sQuery(id+"F17.wireOp",EDGE,"E74.filletArc")])]}),"instanceName":"1"})])],"derivedFrom":makeQuery(id+"F15.boolean.opBoolean","SPLIT",FACE,{"disambiguationData":[TD([subQ1])],"derivedFrom":subQ3})});}
            var Q8;
            {var subQ0=sQuery(id+"F13.wireOp",EDGE,"E64.MirrorCS");var subQ1=makeQuery(id+"F14.opExtrude","SWEPT_FACE",FACE,{"disambiguationData":[OSD([subQ0])]});var subQ2=sQuery(id+"F10.wireOp",EDGE,"E44");var subQ3=makeQuery(id+"F11.boolean.opBoolean","COPY",FACE,{"derivedFrom":makeQuery(id+"F11.opRevolve","SWEPT_FACE",FACE,{"disambiguationData":[OSD([subQ2])]})});Q8=makeQuery(id+"F19.boolean.opBoolean","SPLIT",FACE,{"disambiguationData":[TD([makeQuery(id+"F19.opPattern","COPY",FACE,{"derivedFrom":makeQuery(id+"F18.opExtrude","SWEPT_FACE",FACE,{"disambiguationData":[OSD([sQuery(id+"F17.wireOp",EDGE,"E70")])]}),"instanceName":"1"})])],"derivedFrom":makeQuery(id+"F15.boolean.opBoolean","SPLIT",FACE,{"disambiguationData":[TD([subQ1])],"derivedFrom":subQ3})});}
            var Q9;
            {var subQ0=sQuery(id+"F13.wireOp",EDGE,"E65.MirrorCS");var subQ1=makeQuery(id+"F14.opExtrude","SWEPT_FACE",FACE,{"disambiguationData":[OSD([subQ0])]});var subQ2=sQuery(id+"F10.wireOp",EDGE,"E42");var subQ3=makeQuery(id+"F11.boolean.opBoolean","COPY",FACE,{"derivedFrom":makeQuery(id+"F11.opRevolve","SWEPT_FACE",FACE,{"disambiguationData":[OSD([subQ2])]})});Q9=makeQuery(id+"F19.boolean.opBoolean","SPLIT",FACE,{"disambiguationData":[TD([makeQuery(id+"F19.opPattern","COPY",FACE,{"derivedFrom":makeQuery(id+"F18.opExtrude","SWEPT_FACE",FACE,{"disambiguationData":[OSD([sQuery(id+"F17.wireOp",EDGE,"E70")])]}),"instanceName":"1"})])],"derivedFrom":makeQuery(id+"F15.boolean.opBoolean","SPLIT",FACE,{"disambiguationData":[TD([subQ1])],"derivedFrom":subQ3})});}
            var Q10;
            {var subQ2=sQuery(id+"F10.wireOp",EDGE,"E49.filletArc");var subQ3=makeQuery(id+"F11.boolean.opBoolean","COPY",FACE,{"derivedFrom":makeQuery(id+"F11.opRevolve","SWEPT_FACE",FACE,{"disambiguationData":[OSD([subQ2])]})});var subQ8=sQuery(id+"F13.wireOp",EDGE,"E55");var subQ9=makeQuery(id+"F14.opExtrude","SWEPT_FACE",FACE,{"disambiguationData":[OSD([subQ8])]});Q10=makeQuery(id+"F19.boolean.opBoolean","SPLIT",FACE,{"disambiguationData":[TD([makeQuery(id+"F18.opExtrude","SWEPT_FACE",FACE,{"disambiguationData":[OSD([sQuery(id+"F17.wireOp",EDGE,"E76.MirrorCS")])]})])],"derivedFrom":makeQuery(id+"F15.boolean.opBoolean","SPLIT",FACE,{"disambiguationData":[TD([subQ9])],"derivedFrom":subQ3})});}
            var Q11;
            {var subQ0=sQuery(id+"F13.wireOp",EDGE,"E58");var subQ1=makeQuery(id+"F14.opExtrude","SWEPT_FACE",FACE,{"disambiguationData":[OSD([subQ0])]});var subQ2=sQuery(id+"F10.wireOp",EDGE,"E42");var subQ3=makeQuery(id+"F11.boolean.opBoolean","COPY",FACE,{"derivedFrom":makeQuery(id+"F11.opRevolve","SWEPT_FACE",FACE,{"disambiguationData":[OSD([subQ2])]})});Q11=makeQuery(id+"F19.boolean.opBoolean","SPLIT",FACE,{"disambiguationData":[TD([makeQuery(id+"F18.opExtrude","SWEPT_FACE",FACE,{"disambiguationData":[OSD([sQuery(id+"F17.wireOp",EDGE,"E77.MirrorCS")])]})])],"derivedFrom":makeQuery(id+"F15.boolean.opBoolean","SPLIT",FACE,{"disambiguationData":[TD([subQ1])],"derivedFrom":subQ3})});}
            var Q12;
            {var subQ2=sQuery(id+"F10.wireOp",EDGE,"E49.filletArc");var subQ3=makeQuery(id+"F11.boolean.opBoolean","COPY",FACE,{"derivedFrom":makeQuery(id+"F11.opRevolve","SWEPT_FACE",FACE,{"disambiguationData":[OSD([subQ2])]})});Q12=makeQuery(id+"F19.boolean.opBoolean","SPLIT",FACE,{"disambiguationData":[TD([makeQuery(id+"F18.opExtrude","SWEPT_FACE",FACE,{"disambiguationData":[OSD([sQuery(id+"F17.wireOp",EDGE,"E74.filletArc")])]})])],"derivedFrom":makeQuery(id+"F15.boolean.opBoolean","SPLIT",FACE,{"disambiguationData":[TD([makeQuery(id+"F14.opExtrude","SWEPT_FACE",FACE,{"disambiguationData":[OSD([sQuery(id+"F13.wireOp",EDGE,"E55")])]})])],"derivedFrom":subQ3})});}
            var Q13;
            {var subQ4=sQuery(id+"F10.wireOp",EDGE,"E44");var subQ5=makeQuery(id+"F11.boolean.opBoolean","COPY",FACE,{"derivedFrom":makeQuery(id+"F11.opRevolve","SWEPT_FACE",FACE,{"disambiguationData":[OSD([subQ4])]})});Q13=makeQuery(id+"F19.boolean.opBoolean","SPLIT",FACE,{"disambiguationData":[TD([makeQuery(id+"F18.opExtrude","SWEPT_FACE",FACE,{"disambiguationData":[OSD([sQuery(id+"F17.wireOp",EDGE,"E70")])]})])],"derivedFrom":makeQuery(id+"F15.boolean.opBoolean","SPLIT",FACE,{"disambiguationData":[TD([makeQuery(id+"F14.opExtrude","SWEPT_FACE",FACE,{"disambiguationData":[OSD([sQuery(id+"F13.wireOp",EDGE,"E55")])]})])],"derivedFrom":subQ5})});}
            var Q14;
            {var subQ2=sQuery(id+"F10.wireOp",EDGE,"E42");var subQ3=makeQuery(id+"F11.boolean.opBoolean","COPY",FACE,{"derivedFrom":makeQuery(id+"F11.opRevolve","SWEPT_FACE",FACE,{"disambiguationData":[OSD([subQ2])]})});Q14=makeQuery(id+"F19.boolean.opBoolean","SPLIT",FACE,{"disambiguationData":[TD([makeQuery(id+"F18.opExtrude","SWEPT_FACE",FACE,{"disambiguationData":[OSD([sQuery(id+"F17.wireOp",EDGE,"E70")])]})])],"derivedFrom":makeQuery(id+"F15.boolean.opBoolean","SPLIT",FACE,{"disambiguationData":[TD([makeQuery(id+"F14.opExtrude","SWEPT_FACE",FACE,{"disambiguationData":[OSD([sQuery(id+"F13.wireOp",EDGE,"E58")])]})])],"derivedFrom":subQ3})});}
            var Q15;
            {var subQ0=sQuery(id+"F13.wireOp",EDGE,"E55");var subQ1=makeQuery(id+"F14.opExtrude","SWEPT_FACE",FACE,{"disambiguationData":[OSD([subQ0])]});var subQ2=sQuery(id+"F10.wireOp",EDGE,"E44");var subQ3=makeQuery(id+"F11.boolean.opBoolean","COPY",FACE,{"derivedFrom":makeQuery(id+"F11.opRevolve","SWEPT_FACE",FACE,{"disambiguationData":[OSD([subQ2])]})});Q15=makeQuery(id+"F19.boolean.opBoolean","SPLIT",FACE,{"disambiguationData":[TD([makeQuery(id+"F18.opExtrude","SWEPT_FACE",FACE,{"disambiguationData":[OSD([sQuery(id+"F17.wireOp",EDGE,"E77.MirrorCS")])]})])],"derivedFrom":makeQuery(id+"F15.boolean.opBoolean","SPLIT",FACE,{"disambiguationData":[TD([subQ1])],"derivedFrom":subQ3})});}
            var Q16;
            {var subQ2=sQuery(id+"F10.wireOp",EDGE,"E44");var subQ3=makeQuery(id+"F11.boolean.opBoolean","COPY",FACE,{"derivedFrom":makeQuery(id+"F11.opRevolve","SWEPT_FACE",FACE,{"disambiguationData":[OSD([subQ2])]})});Q16=makeQuery(id+"F19.boolean.opBoolean","SPLIT",FACE,{"disambiguationData":[TD([makeQuery(id+"F19.opPattern","COPY",FACE,{"derivedFrom":makeQuery(id+"F18.opExtrude","SWEPT_FACE",FACE,{"disambiguationData":[OSD([sQuery(id+"F17.wireOp",EDGE,"E77.MirrorCS")])]}),"instanceName":"1"})])],"derivedFrom":makeQuery(id+"F15.boolean.opBoolean","SPLIT",FACE,{"disambiguationData":[TD([makeQuery(id+"F14.opExtrude","SWEPT_FACE",FACE,{"disambiguationData":[OSD([sQuery(id+"F13.wireOp",EDGE,"E64.MirrorCS")])]})])],"derivedFrom":subQ3})});}
            var Q17;
            {var subQ2=sQuery(id+"F13.wireOp",EDGE,"E64.MirrorCS");var subQ3=makeQuery(id+"F15.opPattern","COPY",FACE,{"derivedFrom":makeQuery(id+"F14.opExtrude","SWEPT_FACE",FACE,{"disambiguationData":[OSD([subQ2])]}),"instanceName":"1"});var subQ4=sQuery(id+"F10.wireOp",EDGE,"E44");var subQ5=makeQuery(id+"F11.boolean.opBoolean","COPY",FACE,{"derivedFrom":makeQuery(id+"F11.opRevolve","SWEPT_FACE",FACE,{"disambiguationData":[OSD([subQ4])]})});Q17=makeQuery(id+"F19.boolean.opBoolean","SPLIT",FACE,{"disambiguationData":[TD([makeQuery(id+"F19.opPattern","COPY",FACE,{"derivedFrom":makeQuery(id+"F18.opExtrude","SWEPT_FACE",FACE,{"disambiguationData":[OSD([sQuery(id+"F17.wireOp",EDGE,"E70")])]}),"instanceName":"2"})])],"derivedFrom":makeQuery(id+"F15.boolean.opBoolean","SPLIT",FACE,{"disambiguationData":[TD([subQ3])],"derivedFrom":subQ5})});}
            var Q18;
            {var subQ0=sQuery(id+"F13.wireOp",EDGE,"E63.MirrorCS");var subQ1=makeQuery(id+"F15.opPattern","COPY",FACE,{"derivedFrom":makeQuery(id+"F14.opExtrude","SWEPT_FACE",FACE,{"disambiguationData":[OSD([subQ0])]}),"instanceName":"1"});var subQ2=sQuery(id+"F10.wireOp",EDGE,"E49.filletArc");var subQ3=makeQuery(id+"F11.boolean.opBoolean","COPY",FACE,{"derivedFrom":makeQuery(id+"F11.opRevolve","SWEPT_FACE",FACE,{"disambiguationData":[OSD([subQ2])]})});Q18=makeQuery(id+"F19.boolean.opBoolean","SPLIT",FACE,{"disambiguationData":[TD([makeQuery(id+"F19.opPattern","COPY",FACE,{"derivedFrom":makeQuery(id+"F18.opExtrude","SWEPT_FACE",FACE,{"disambiguationData":[OSD([sQuery(id+"F17.wireOp",EDGE,"E70")])]}),"instanceName":"2"})])],"derivedFrom":makeQuery(id+"F15.boolean.opBoolean","SPLIT",FACE,{"disambiguationData":[TD([subQ1])],"derivedFrom":subQ3})});}
            var Q19;
            {var subQ0=sQuery(id+"F13.wireOp",EDGE,"E65.MirrorCS");var subQ1=makeQuery(id+"F15.opPattern","COPY",FACE,{"derivedFrom":makeQuery(id+"F14.opExtrude","SWEPT_FACE",FACE,{"disambiguationData":[OSD([subQ0])]}),"instanceName":"1"});var subQ2=sQuery(id+"F10.wireOp",EDGE,"E42");var subQ3=makeQuery(id+"F11.boolean.opBoolean","COPY",FACE,{"derivedFrom":makeQuery(id+"F11.opRevolve","SWEPT_FACE",FACE,{"disambiguationData":[OSD([subQ2])]})});Q19=makeQuery(id+"F19.boolean.opBoolean","SPLIT",FACE,{"disambiguationData":[TD([makeQuery(id+"F19.opPattern","COPY",FACE,{"derivedFrom":makeQuery(id+"F18.opExtrude","SWEPT_FACE",FACE,{"disambiguationData":[OSD([sQuery(id+"F17.wireOp",EDGE,"E70")])]}),"instanceName":"2"})])],"derivedFrom":makeQuery(id+"F15.boolean.opBoolean","SPLIT",FACE,{"disambiguationData":[TD([subQ1])],"derivedFrom":subQ3})});}
            var Q20;
            {var subQ2=sQuery(id+"F10.wireOp",EDGE,"E42");var subQ3=makeQuery(id+"F11.boolean.opBoolean","COPY",FACE,{"derivedFrom":makeQuery(id+"F11.opRevolve","SWEPT_FACE",FACE,{"disambiguationData":[OSD([subQ2])]})});Q20=makeQuery(id+"F19.boolean.opBoolean","SPLIT",FACE,{"disambiguationData":[TD([makeQuery(id+"F19.opPattern","COPY",FACE,{"derivedFrom":makeQuery(id+"F18.opExtrude","SWEPT_FACE",FACE,{"disambiguationData":[OSD([sQuery(id+"F17.wireOp",EDGE,"E77.MirrorCS")])]}),"instanceName":"2"})])],"derivedFrom":makeQuery(id+"F15.boolean.opBoolean","SPLIT",FACE,{"disambiguationData":[TD([makeQuery(id+"F15.opPattern","COPY",FACE,{"derivedFrom":makeQuery(id+"F14.opExtrude","SWEPT_FACE",FACE,{"disambiguationData":[OSD([sQuery(id+"F13.wireOp",EDGE,"E65.MirrorCS")])]}),"instanceName":"1"})])],"derivedFrom":subQ3})});}
            var Q21;
            {var subQ4=sQuery(id+"F10.wireOp",EDGE,"E44");var subQ5=makeQuery(id+"F11.boolean.opBoolean","COPY",FACE,{"derivedFrom":makeQuery(id+"F11.opRevolve","SWEPT_FACE",FACE,{"disambiguationData":[OSD([subQ4])]})});Q21=makeQuery(id+"F19.boolean.opBoolean","SPLIT",FACE,{"disambiguationData":[TD([makeQuery(id+"F19.opPattern","COPY",FACE,{"derivedFrom":makeQuery(id+"F18.opExtrude","SWEPT_FACE",FACE,{"disambiguationData":[OSD([sQuery(id+"F17.wireOp",EDGE,"E77.MirrorCS")])]}),"instanceName":"2"})])],"derivedFrom":makeQuery(id+"F15.boolean.opBoolean","SPLIT",FACE,{"disambiguationData":[TD([makeQuery(id+"F15.opPattern","COPY",FACE,{"derivedFrom":makeQuery(id+"F14.opExtrude","SWEPT_FACE",FACE,{"disambiguationData":[OSD([sQuery(id+"F13.wireOp",EDGE,"E64.MirrorCS")])]}),"instanceName":"1"})])],"derivedFrom":subQ5})});}
            var Q22;
            {var subQ6=sQuery(id+"F10.wireOp",EDGE,"E49.filletArc");var subQ7=makeQuery(id+"F11.boolean.opBoolean","COPY",FACE,{"derivedFrom":makeQuery(id+"F11.opRevolve","SWEPT_FACE",FACE,{"disambiguationData":[OSD([subQ6])]})});Q22=makeQuery(id+"F19.boolean.opBoolean","SPLIT",FACE,{"disambiguationData":[TD([makeQuery(id+"F19.opPattern","COPY",FACE,{"derivedFrom":makeQuery(id+"F18.opExtrude","SWEPT_FACE",FACE,{"disambiguationData":[OSD([sQuery(id+"F17.wireOp",EDGE,"E76.MirrorCS")])]}),"instanceName":"2"})])],"derivedFrom":makeQuery(id+"F15.boolean.opBoolean","SPLIT",FACE,{"disambiguationData":[TD([makeQuery(id+"F15.opPattern","COPY",FACE,{"derivedFrom":makeQuery(id+"F14.opExtrude","SWEPT_FACE",FACE,{"disambiguationData":[OSD([sQuery(id+"F13.wireOp",EDGE,"E63.MirrorCS")])]}),"instanceName":"1"})])],"derivedFrom":subQ7})});}
            var Q23;
            {var subQ2=sQuery(id+"F10.wireOp",EDGE,"E44");var subQ3=makeQuery(id+"F11.boolean.opBoolean","COPY",FACE,{"derivedFrom":makeQuery(id+"F11.opRevolve","SWEPT_FACE",FACE,{"disambiguationData":[OSD([subQ2])]})});Q23=makeQuery(id+"F19.boolean.opBoolean","SPLIT",FACE,{"disambiguationData":[TD([makeQuery(id+"F19.opPattern","COPY",FACE,{"derivedFrom":makeQuery(id+"F18.opExtrude","SWEPT_FACE",FACE,{"disambiguationData":[OSD([sQuery(id+"F17.wireOp",EDGE,"E77.MirrorCS")])]}),"instanceName":"3"})])],"derivedFrom":makeQuery(id+"F15.boolean.opBoolean","SPLIT",FACE,{"disambiguationData":[TD([makeQuery(id+"F15.opPattern","COPY",FACE,{"derivedFrom":makeQuery(id+"F14.opExtrude","SWEPT_FACE",FACE,{"disambiguationData":[OSD([sQuery(id+"F13.wireOp",EDGE,"E64.MirrorCS")])]}),"instanceName":"2"})])],"derivedFrom":subQ3})});}
            var Q24;
            {var subQ0=sQuery(id+"F13.wireOp",EDGE,"E63.MirrorCS");var subQ1=makeQuery(id+"F15.opPattern","COPY",FACE,{"derivedFrom":makeQuery(id+"F14.opExtrude","SWEPT_FACE",FACE,{"disambiguationData":[OSD([subQ0])]}),"instanceName":"3"});var subQ2=sQuery(id+"F10.wireOp",EDGE,"E49.filletArc");var subQ3=makeQuery(id+"F11.boolean.opBoolean","COPY",FACE,{"derivedFrom":makeQuery(id+"F11.opRevolve","SWEPT_FACE",FACE,{"disambiguationData":[OSD([subQ2])]})});Q24=makeQuery(id+"F19.boolean.opBoolean","SPLIT",FACE,{"disambiguationData":[TD([makeQuery(id+"F19.opPattern","COPY",FACE,{"derivedFrom":makeQuery(id+"F18.opExtrude","SWEPT_FACE",FACE,{"disambiguationData":[OSD([sQuery(id+"F17.wireOp",EDGE,"E70")])]}),"instanceName":"4"})])],"derivedFrom":makeQuery(id+"F15.boolean.opBoolean","SPLIT",FACE,{"disambiguationData":[TD([subQ1])],"derivedFrom":subQ3})});}
            var Q25;
            {var subQ4=sQuery(id+"F10.wireOp",EDGE,"E44");var subQ5=makeQuery(id+"F11.boolean.opBoolean","COPY",FACE,{"derivedFrom":makeQuery(id+"F11.opRevolve","SWEPT_FACE",FACE,{"disambiguationData":[OSD([subQ4])]})});var subQ6=sQuery(id+"F13.wireOp",EDGE,"E64.MirrorCS");var subQ7=makeQuery(id+"F15.opPattern","COPY",FACE,{"derivedFrom":makeQuery(id+"F14.opExtrude","SWEPT_FACE",FACE,{"disambiguationData":[OSD([subQ6])]}),"instanceName":"3"});Q25=makeQuery(id+"F19.boolean.opBoolean","SPLIT",FACE,{"disambiguationData":[TD([makeQuery(id+"F19.opPattern","COPY",FACE,{"derivedFrom":makeQuery(id+"F18.opExtrude","SWEPT_FACE",FACE,{"disambiguationData":[OSD([sQuery(id+"F17.wireOp",EDGE,"E70")])]}),"instanceName":"4"})])],"derivedFrom":makeQuery(id+"F15.boolean.opBoolean","SPLIT",FACE,{"disambiguationData":[TD([subQ7])],"derivedFrom":subQ5})});}
            var Q26;
            {var subQ0=sQuery(id+"F13.wireOp",EDGE,"E65.MirrorCS");var subQ1=makeQuery(id+"F15.opPattern","COPY",FACE,{"derivedFrom":makeQuery(id+"F14.opExtrude","SWEPT_FACE",FACE,{"disambiguationData":[OSD([subQ0])]}),"instanceName":"3"});var subQ2=sQuery(id+"F10.wireOp",EDGE,"E42");var subQ3=makeQuery(id+"F11.boolean.opBoolean","COPY",FACE,{"derivedFrom":makeQuery(id+"F11.opRevolve","SWEPT_FACE",FACE,{"disambiguationData":[OSD([subQ2])]})});Q26=makeQuery(id+"F19.boolean.opBoolean","SPLIT",FACE,{"disambiguationData":[TD([makeQuery(id+"F19.opPattern","COPY",FACE,{"derivedFrom":makeQuery(id+"F18.opExtrude","SWEPT_FACE",FACE,{"disambiguationData":[OSD([sQuery(id+"F17.wireOp",EDGE,"E70")])]}),"instanceName":"4"})])],"derivedFrom":makeQuery(id+"F15.boolean.opBoolean","SPLIT",FACE,{"disambiguationData":[TD([subQ1])],"derivedFrom":subQ3})});}
            var Q27;
            {var subQ2=sQuery(id+"F10.wireOp",EDGE,"E42");var subQ3=makeQuery(id+"F11.boolean.opBoolean","COPY",FACE,{"derivedFrom":makeQuery(id+"F11.opRevolve","SWEPT_FACE",FACE,{"disambiguationData":[OSD([subQ2])]})});Q27=makeQuery(id+"F19.boolean.opBoolean","SPLIT",FACE,{"disambiguationData":[TD([makeQuery(id+"F19.opPattern","COPY",FACE,{"derivedFrom":makeQuery(id+"F18.opExtrude","SWEPT_FACE",FACE,{"disambiguationData":[OSD([sQuery(id+"F17.wireOp",EDGE,"E77.MirrorCS")])]}),"instanceName":"4"})])],"derivedFrom":makeQuery(id+"F15.boolean.opBoolean","SPLIT",FACE,{"disambiguationData":[TD([makeQuery(id+"F15.opPattern","COPY",FACE,{"derivedFrom":makeQuery(id+"F14.opExtrude","SWEPT_FACE",FACE,{"disambiguationData":[OSD([sQuery(id+"F13.wireOp",EDGE,"E65.MirrorCS")])]}),"instanceName":"3"})])],"derivedFrom":subQ3})});}
            var Q28;
            {var subQ4=sQuery(id+"F10.wireOp",EDGE,"E44");var subQ5=makeQuery(id+"F11.boolean.opBoolean","COPY",FACE,{"derivedFrom":makeQuery(id+"F11.opRevolve","SWEPT_FACE",FACE,{"disambiguationData":[OSD([subQ4])]})});Q28=makeQuery(id+"F19.boolean.opBoolean","SPLIT",FACE,{"disambiguationData":[TD([makeQuery(id+"F19.opPattern","COPY",FACE,{"derivedFrom":makeQuery(id+"F18.opExtrude","SWEPT_FACE",FACE,{"disambiguationData":[OSD([sQuery(id+"F17.wireOp",EDGE,"E77.MirrorCS")])]}),"instanceName":"4"})])],"derivedFrom":makeQuery(id+"F15.boolean.opBoolean","SPLIT",FACE,{"disambiguationData":[TD([makeQuery(id+"F15.opPattern","COPY",FACE,{"derivedFrom":makeQuery(id+"F14.opExtrude","SWEPT_FACE",FACE,{"disambiguationData":[OSD([sQuery(id+"F13.wireOp",EDGE,"E64.MirrorCS")])]}),"instanceName":"3"})])],"derivedFrom":subQ5})});}
            var Q29;
            {var subQ2=sQuery(id+"F10.wireOp",EDGE,"E49.filletArc");var subQ3=makeQuery(id+"F11.boolean.opBoolean","COPY",FACE,{"derivedFrom":makeQuery(id+"F11.opRevolve","SWEPT_FACE",FACE,{"disambiguationData":[OSD([subQ2])]})});Q29=makeQuery(id+"F19.boolean.opBoolean","SPLIT",FACE,{"disambiguationData":[TD([makeQuery(id+"F19.opPattern","COPY",FACE,{"derivedFrom":makeQuery(id+"F18.opExtrude","SWEPT_FACE",FACE,{"disambiguationData":[OSD([sQuery(id+"F17.wireOp",EDGE,"E76.MirrorCS")])]}),"instanceName":"4"})])],"derivedFrom":makeQuery(id+"F15.boolean.opBoolean","SPLIT",FACE,{"disambiguationData":[TD([makeQuery(id+"F15.opPattern","COPY",FACE,{"derivedFrom":makeQuery(id+"F14.opExtrude","SWEPT_FACE",FACE,{"disambiguationData":[OSD([sQuery(id+"F13.wireOp",EDGE,"E63.MirrorCS")])]}),"instanceName":"3"})])],"derivedFrom":subQ3})});}
            var Q30;
            {var subQ1=makeQuery(id+"F11.boolean.opBoolean","COPY",FACE,{"derivedFrom":makeQuery(id+"F11.opRevolve","SWEPT_FACE",FACE,{"disambiguationData":[OSD([sQuery(id+"F10.wireOp",EDGE,"E42")])]})});var subQ3=makeQuery(id+"F15.opPattern","COPY",FACE,{"derivedFrom":makeQuery(id+"F14.opExtrude","SWEPT_FACE",FACE,{"disambiguationData":[OSD([sQuery(id+"F13.wireOp",EDGE,"E65.MirrorCS")])]}),"instanceName":"4"});Q30=makeQuery(id+"F19.boolean.opBoolean","SPLIT",FACE,{"disambiguationData":[TD([makeQuery(id+"F19.opPattern","COPY",FACE,{"derivedFrom":makeQuery(id+"F18.opExtrude","SWEPT_FACE",FACE,{"disambiguationData":[OSD([sQuery(id+"F17.wireOp",EDGE,"E70")])]}),"instanceName":"5"})])],"derivedFrom":makeQuery(id+"F15.boolean.opBoolean","SPLIT",FACE,{"disambiguationData":[TD([subQ3])],"derivedFrom":subQ1})});}
            var Q31;
            {var subQ2=sQuery(id+"F13.wireOp",EDGE,"E63.MirrorCS");var subQ3=makeQuery(id+"F15.opPattern","COPY",FACE,{"derivedFrom":makeQuery(id+"F14.opExtrude","SWEPT_FACE",FACE,{"disambiguationData":[OSD([subQ2])]}),"instanceName":"4"});var subQ4=makeQuery(id+"F15.opPattern","COPY",FACE,{"derivedFrom":makeQuery(id+"F14.opExtrude","SWEPT_FACE",FACE,{"disambiguationData":[OSD([sQuery(id+"F13.wireOp",EDGE,"E64.MirrorCS")])]}),"instanceName":"4"});Q31=makeQuery(id+"F19.boolean.opBoolean","SPLIT",FACE,{"disambiguationData":[TD([makeQuery(id+"F15.boolean.opBoolean","COPY",FACE,{"derivedFrom":subQ4})])],"derivedFrom":makeQuery(id+"F15.boolean.opBoolean","SPLIT",FACE,{"disambiguationData":[TD([subQ3])],"derivedFrom":makeQuery(id+"F11.boolean.opBoolean","COPY",FACE,{"derivedFrom":makeQuery(id+"F11.opRevolve","SWEPT_FACE",FACE,{"disambiguationData":[OSD([sQuery(id+"F10.wireOp",EDGE,"E49.filletArc")])]})})})});}
            var Q32;
            {var subQ1=makeQuery(id+"F11.boolean.opBoolean","COPY",FACE,{"derivedFrom":makeQuery(id+"F11.opRevolve","SWEPT_FACE",FACE,{"disambiguationData":[OSD([sQuery(id+"F10.wireOp",EDGE,"E42")])]})});Q32=makeQuery(id+"F19.boolean.opBoolean","SPLIT",FACE,{"disambiguationData":[TD([makeQuery(id+"F19.opPattern","COPY",FACE,{"derivedFrom":makeQuery(id+"F18.opExtrude","SWEPT_FACE",FACE,{"disambiguationData":[OSD([sQuery(id+"F17.wireOp",EDGE,"E77.MirrorCS")])]}),"instanceName":"5"})])],"derivedFrom":makeQuery(id+"F15.boolean.opBoolean","SPLIT",FACE,{"disambiguationData":[TD([makeQuery(id+"F15.opPattern","COPY",FACE,{"derivedFrom":makeQuery(id+"F14.opExtrude","SWEPT_FACE",FACE,{"disambiguationData":[OSD([sQuery(id+"F13.wireOp",EDGE,"E65.MirrorCS")])]}),"instanceName":"4"})])],"derivedFrom":subQ1})});}
            var Q33;
            {var subQ4=makeQuery(id+"F15.opPattern","COPY",FACE,{"derivedFrom":makeQuery(id+"F14.opExtrude","SWEPT_FACE",FACE,{"disambiguationData":[OSD([sQuery(id+"F13.wireOp",EDGE,"E55")])]}),"instanceName":"5"});Q33=makeQuery(id+"F19.boolean.opBoolean","SPLIT",FACE,{"disambiguationData":[TD([makeQuery(id+"F15.boolean.opBoolean","COPY",FACE,{"derivedFrom":subQ4})])],"derivedFrom":makeQuery(id+"F15.boolean.opBoolean","SPLIT",FACE,{"disambiguationData":[TD([makeQuery(id+"F15.opPattern","COPY",FACE,{"derivedFrom":makeQuery(id+"F14.opExtrude","SWEPT_FACE",FACE,{"disambiguationData":[OSD([sQuery(id+"F13.wireOp",EDGE,"E63.MirrorCS")])]}),"instanceName":"4"})])],"derivedFrom":makeQuery(id+"F11.boolean.opBoolean","COPY",FACE,{"derivedFrom":makeQuery(id+"F11.opRevolve","SWEPT_FACE",FACE,{"disambiguationData":[OSD([sQuery(id+"F10.wireOp",EDGE,"E49.filletArc")])]})})})});}
            var Q34;
            {var subQ4=sQuery(id+"F10.wireOp",EDGE,"E44");var subQ5=makeQuery(id+"F11.boolean.opBoolean","COPY",FACE,{"derivedFrom":makeQuery(id+"F11.opRevolve","SWEPT_FACE",FACE,{"disambiguationData":[OSD([subQ4])]})});Q34=makeQuery(id+"F19.boolean.opBoolean","SPLIT",FACE,{"disambiguationData":[TD([makeQuery(id+"F19.opPattern","COPY",FACE,{"derivedFrom":makeQuery(id+"F18.opExtrude","SWEPT_FACE",FACE,{"disambiguationData":[OSD([sQuery(id+"F17.wireOp",EDGE,"E77.MirrorCS")])]}),"instanceName":"5"})])],"derivedFrom":makeQuery(id+"F15.boolean.opBoolean","SPLIT",FACE,{"disambiguationData":[TD([makeQuery(id+"F15.opPattern","COPY",FACE,{"derivedFrom":makeQuery(id+"F14.opExtrude","SWEPT_FACE",FACE,{"disambiguationData":[OSD([sQuery(id+"F13.wireOp",EDGE,"E64.MirrorCS")])]}),"instanceName":"4"})])],"derivedFrom":subQ5})});}
            var Q35;
            {var subQ0=sQuery(id+"F13.wireOp",EDGE,"E64.MirrorCS");var subQ1=makeQuery(id+"F15.opPattern","COPY",FACE,{"derivedFrom":makeQuery(id+"F14.opExtrude","SWEPT_FACE",FACE,{"disambiguationData":[OSD([subQ0])]}),"instanceName":"4"});var subQ2=sQuery(id+"F10.wireOp",EDGE,"E44");var subQ3=makeQuery(id+"F11.boolean.opBoolean","COPY",FACE,{"derivedFrom":makeQuery(id+"F11.opRevolve","SWEPT_FACE",FACE,{"disambiguationData":[OSD([subQ2])]})});Q35=makeQuery(id+"F19.boolean.opBoolean","SPLIT",FACE,{"disambiguationData":[TD([makeQuery(id+"F19.opPattern","COPY",FACE,{"derivedFrom":makeQuery(id+"F18.opExtrude","SWEPT_FACE",FACE,{"disambiguationData":[OSD([sQuery(id+"F17.wireOp",EDGE,"E70")])]}),"instanceName":"5"})])],"derivedFrom":makeQuery(id+"F15.boolean.opBoolean","SPLIT",FACE,{"disambiguationData":[TD([subQ1])],"derivedFrom":subQ3})});}
            var Q36;
            {var subQ0=makeQuery(id+"F18.opExtrude","SWEPT_FACE",FACE,{"disambiguationData":[OSD([sQuery(id+"F17.wireOp",EDGE,"E72"),sQuery(id+"F17.wireOp",EDGE,"E79.MirrorCS")])]});var subQ1=makeQuery(id+"F14.opExtrude","SWEPT_FACE",FACE,{"disambiguationData":[OSD([sQuery(id+"F13.wireOp",EDGE,"E57"),sQuery(id+"F13.wireOp",EDGE,"E66.MirrorCS")])]});Q36=makeQuery(id+"F19.boolean.opBoolean","MERGE",FACE,{"derivedFrom":[makeQuery(id+"F15.boolean.opBoolean","MERGE",FACE,{"derivedFrom":[makeQuery(id+"F11.boolean.opBoolean","COPY",FACE,{"derivedFrom":makeQuery(id+"F11.opRevolve","SWEPT_FACE",FACE,{"disambiguationData":[OSD([sQuery(id+"F10.wireOp",EDGE,"E41")])]})}),subQ1,makeQuery(id+"F15.opPattern","COPY",FACE,{"derivedFrom":subQ1,"instanceName":"1"}),makeQuery(id+"F15.opPattern","COPY",FACE,{"derivedFrom":subQ1,"instanceName":"2"}),makeQuery(id+"F15.opPattern","COPY",FACE,{"derivedFrom":subQ1,"instanceName":"3"}),makeQuery(id+"F15.opPattern","COPY",FACE,{"derivedFrom":subQ1,"instanceName":"4"}),makeQuery(id+"F15.opPattern","COPY",FACE,{"derivedFrom":subQ1,"instanceName":"5"})]}),subQ0,makeQuery(id+"F19.opPattern","COPY",FACE,{"derivedFrom":subQ0,"instanceName":"1"}),makeQuery(id+"F19.opPattern","COPY",FACE,{"derivedFrom":subQ0,"instanceName":"2"}),makeQuery(id+"F19.opPattern","COPY",FACE,{"derivedFrom":subQ0,"instanceName":"3"}),makeQuery(id+"F19.opPattern","COPY",FACE,{"derivedFrom":subQ0,"instanceName":"4"}),makeQuery(id+"F19.opPattern","COPY",FACE,{"derivedFrom":subQ0,"instanceName":"5"})]});}
            var Q37;
            Q37=makeQuery(id+"F11.boolean.opBoolean","COPY",FACE,{"derivedFrom":makeQuery(id+"F11.opRevolve","SWEPT_FACE",FACE,{"disambiguationData":[OSD([sQuery(id+"F10.wireOp",EDGE,"E50")])]})});
            fillet(context, id + "F20", {"entities" : qUnion([Q0, Q1, Q2, Q3, Q4, Q5, Q6, Q7, Q8, Q9, Q10, Q11, Q12, Q13, Q14, Q15, Q16, Q17, Q18, Q19, Q20, Q21, Q22, Q23, Q24, Q25, Q26, Q27, Q28, Q29, Q30, Q31, Q32, Q33, Q34, Q35, Q36, Q37]), "radius" : 1.37 * mm, "tangentPropagation" : true, "allowEdgeOverflow" : false});
        }
        {
            var Q0;
            Q0=qCreatedBy(makeId("Front.planeOp"),FACE);
            var sketch = newSketch(context, id + "F21", { "sketchPlane" : qUnion([Q0])});
            skLineSegment(sketch, "E80", {"start": v(3, 16.87) * mm, "end": v(25.86, 16.87) * mm});
            skLineSegment(sketch, "E81", {"start": v(26.48, 14.7) * mm, "end": v(15.7, 7.98) * mm});
            skPoint(sketch, "E81.endSnap0", {"position": v(0.5, 16.87) * mm});
            skPoint(sketch, "E82.visualSharp", {"position": v(29.94, 16.87) * mm});
            skArc(sketch, "E82.filletArc", {"start": v(26.48, 14.7) * mm, "mid": v(26.98, 16.02) * mm, "end": v(25.86, 16.87) * mm});
            skPoint(sketch, "E83.orphan", {"position": v(7.96, 7.98) * mm});
            skLineSegment(sketch, "E84", {"start": v(15.7, 7.98) * mm, "end": v(7.96, 7.98) * mm});
            skLineSegment(sketch, "E85", {"start": v(7.96, 7.98) * mm, "end": v(2.1, 14.95) * mm});
            skArc(sketch, "E86.filletArc", {"start": v(3, 16.87) * mm, "mid": v(1.94, 16.2) * mm, "end": v(2.1, 14.95) * mm});
            skSolve(sketch);
        }
        {
            var Q0;
            Q0=qSketchRegion(id+"F21",true);
            var Q1;
            Q1=sQuery(id+"F10.wireOp",EDGE,"E46");
            revolve(context, id + "F22", {"operationType" : NewBodyOperationType.REMOVE, "entities" : qUnion([Q0]), "axis" : qUnion([Q1]), "revolveType" : RevolveType.FULL, "oppositeDirection" : true});
        }
    });
